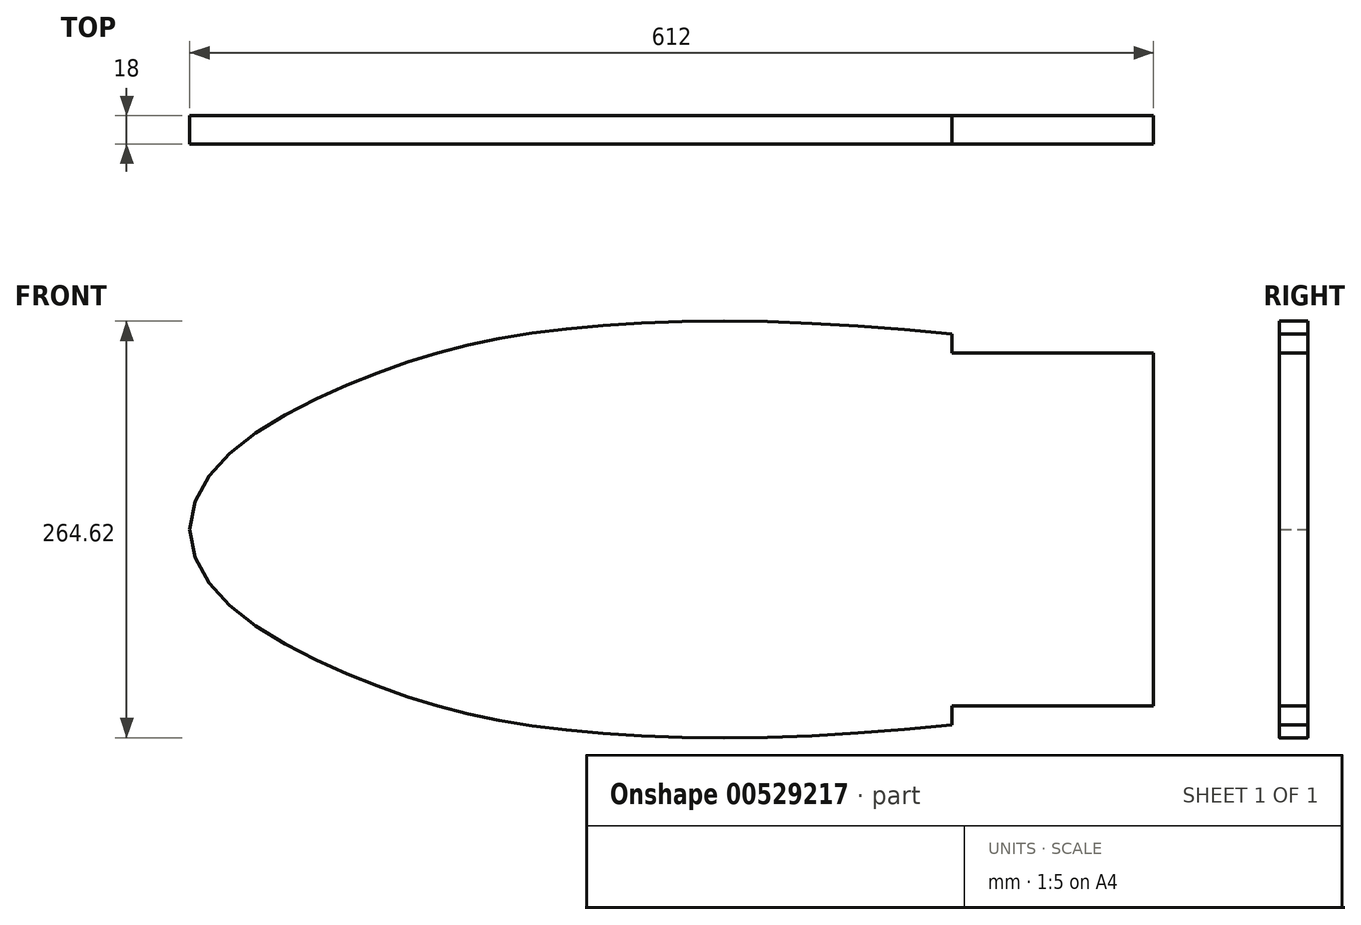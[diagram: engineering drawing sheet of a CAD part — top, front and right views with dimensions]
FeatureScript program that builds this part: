
annotation { "Feature Type Name" : "Feature", "Feature Type Description" : "" }
export const myFeature = defineFeature(function(context is Context, id is Id, definition is map)
    precondition{}
    {
        {
            var Q0;
            Q0=qCreatedBy(makeId("Front.planeOp"),FACE);
            var sketch = newSketch(context, id + "F0", { "sketchPlane" : qUnion([Q0])});
            skLineSegment(sketch, "E0", {"start": v(-355.6, 0) * mm, "end": v(355.6, 0) * mm, "construction": true});
            skLineSegment(sketch, "E1.0.1.0", {"start": v(-355.6, 50.8) * mm, "end": v(355.6, 50.8) * mm, "construction": true});
            skLineSegment(sketch, "E1.0.2.0", {"start": v(-355.6, 101.6) * mm, "end": v(355.6, 101.6) * mm, "construction": true});
            skLineSegment(sketch, "E1.0.3.0", {"start": v(-355.6, 152.4) * mm, "end": v(355.6, 152.4) * mm, "construction": true});
            skLineSegment(sketch, "E1.0.4.0", {"start": v(-355.6, 203.2) * mm, "end": v(355.6, 203.2) * mm, "construction": true});
            skLineSegment(sketch, "E1.0.5.0", {"start": v(-355.6, 254) * mm, "end": v(355.6, 254) * mm, "construction": true});
            skLineSegment(sketch, "E1.direction1", {"start": v(-355.6, 0) * mm, "end": v(-330.6, 0) * mm, "construction": true});
            skLineSegment(sketch, "E1.direction2", {"start": v(-355.6, 0) * mm, "end": v(-355.6, 50.8) * mm, "construction": true});
            skLineSegment(sketch, "E2.0.1.0", {"start": v(-355.6, -50.8) * mm, "end": v(355.6, -50.8) * mm, "construction": true});
            skLineSegment(sketch, "E2.0.2.0", {"start": v(-355.6, -101.6) * mm, "end": v(355.6, -101.6) * mm, "construction": true});
            skLineSegment(sketch, "E2.0.3.0", {"start": v(-355.6, -152.4) * mm, "end": v(355.6, -152.4) * mm, "construction": true});
            skLineSegment(sketch, "E2.0.4.0", {"start": v(-355.6, -203.2) * mm, "end": v(355.6, -203.2) * mm, "construction": true});
            skLineSegment(sketch, "E2.0.5.0", {"start": v(-355.6, -254) * mm, "end": v(355.6, -254) * mm, "construction": true});
            skLineSegment(sketch, "E2.direction1", {"start": v(-355.6, 0) * mm, "end": v(0, 0) * mm, "construction": true});
            skLineSegment(sketch, "E2.direction2", {"start": v(-355.6, 0) * mm, "end": v(-355.6, -50.8) * mm, "construction": true});
            skLineSegment(sketch, "E3", {"start": v(0, 254) * mm, "end": v(0, -254) * mm, "construction": true});
            skLineSegment(sketch, "E4.1.0.0", {"start": v(50.8, 254) * mm, "end": v(50.8, -254) * mm, "construction": true});
            skLineSegment(sketch, "E4.2.0.0", {"start": v(101.6, 254) * mm, "end": v(101.6, -254) * mm, "construction": true});
            skLineSegment(sketch, "E4.3.0.0", {"start": v(152.4, 254) * mm, "end": v(152.4, -254) * mm, "construction": true});
            skLineSegment(sketch, "E4.4.0.0", {"start": v(203.2, 254) * mm, "end": v(203.2, -254) * mm, "construction": true});
            skLineSegment(sketch, "E4.5.0.0", {"start": v(254, 254) * mm, "end": v(254, -254) * mm, "construction": true});
            skLineSegment(sketch, "E4.6.0.0", {"start": v(304.8, 254) * mm, "end": v(304.8, -254) * mm, "construction": true});
            skLineSegment(sketch, "E4.7.0.0", {"start": v(355.6, 254) * mm, "end": v(355.6, -254) * mm, "construction": true});
            skLineSegment(sketch, "E4.direction1", {"start": v(0, -254) * mm, "end": v(50.8, -254) * mm, "construction": true});
            skLineSegment(sketch, "E5.1.0.0", {"start": v(-50.8, 254) * mm, "end": v(-50.8, -254) * mm, "construction": true});
            skLineSegment(sketch, "E5.2.0.0", {"start": v(-101.6, 254) * mm, "end": v(-101.6, -254) * mm, "construction": true});
            skLineSegment(sketch, "E5.3.0.0", {"start": v(-152.4, 254) * mm, "end": v(-152.4, -254) * mm, "construction": true});
            skLineSegment(sketch, "E5.4.0.0", {"start": v(-203.2, 254) * mm, "end": v(-203.2, -254) * mm, "construction": true});
            skLineSegment(sketch, "E5.5.0.0", {"start": v(-254, 254) * mm, "end": v(-254, -254) * mm, "construction": true});
            skLineSegment(sketch, "E5.6.0.0", {"start": v(-304.8, 254) * mm, "end": v(-304.8, -254) * mm, "construction": true});
            skLineSegment(sketch, "E5.7.0.0", {"start": v(-355.6, 254) * mm, "end": v(-355.6, -254) * mm, "construction": true});
            skLineSegment(sketch, "E5.direction1", {"start": v(0, -254) * mm, "end": v(-50.8, -254) * mm, "construction": true});
            skLineSegment(sketch, "E6", {"start": v(-317, -217) * mm, "end": v(295, -217) * mm});
            skLineSegment(sketch, "E7", {"start": v(295, -217) * mm, "end": v(295, -105) * mm});
            skLineSegment(sketch, "E8", {"start": v(295, -105) * mm, "end": v(167, -105) * mm});
            skLineSegment(sketch, "E9", {"start": v(167, -105) * mm, "end": v(167, -93) * mm});
            skFitSpline(sketch, "E10", {"points": [v(167, -93) * mm, v(-84.5, -90.36) * mm, v(-223.77, -128.3) * mm, v(-317, -217) * mm], "startDerivative": vector(-695.8, 76.43) * mm, "endDerivative": vector(-7.53, -432) * mm});
            skFitSpline(sketch, "E11.MirrorCS", {"points": [v(167, -341) * mm, v(-84.5, -343.64) * mm, v(-223.77, -305.7) * mm, v(-317, -217) * mm], "startDerivative": vector(-695.8, -76.43) * mm, "endDerivative": vector(-7.53, 432) * mm});
            skLineSegment(sketch, "E12.MirrorCS", {"start": v(167, -329) * mm, "end": v(167, -341) * mm});
            skLineSegment(sketch, "E13.MirrorCS", {"start": v(295, -329) * mm, "end": v(167, -329) * mm});
            skLineSegment(sketch, "E14.MirrorCS", {"start": v(295, -217) * mm, "end": v(295, -329) * mm});
            skSolve(sketch);
        }
        {
            var Q0;
            Q0=makeQuery(id+"F0.imprint","IMPRINT",FACE,{"disambiguationData":[TD([[makeQuery(id+"F0.imprint","IMPRINT",EDGE,{"derivedFrom":sQuery(id+"F0.wireOp",EDGE,"E6")}),-1.0]])]});
            var Q1;
            Q1=makeQuery(id+"F0.imprint","IMPRINT",FACE,{"disambiguationData":[TD([[makeQuery(id+"F0.imprint","IMPRINT",EDGE,{"derivedFrom":sQuery(id+"F0.wireOp",EDGE,"E6")}),1.0]])]});
            extrude(context, id + "F1", {"entities" : qUnion([Q0, Q1]), "depth" : 18 * mm, "offsetDistance" : 25 * mm});
        }
    });
